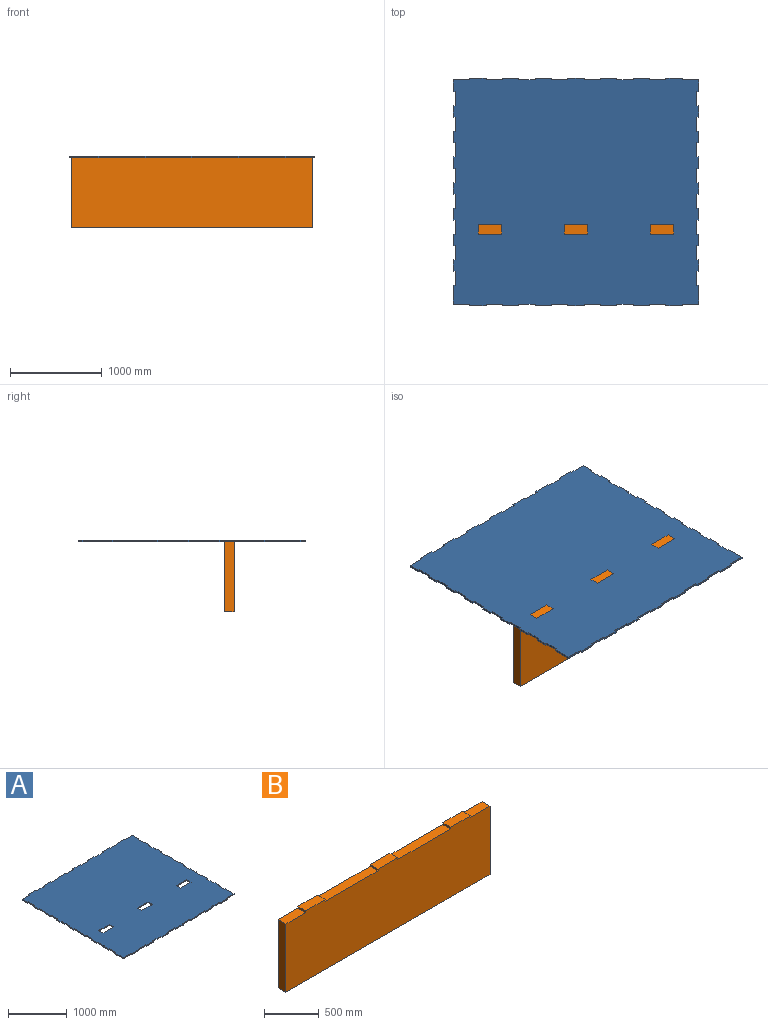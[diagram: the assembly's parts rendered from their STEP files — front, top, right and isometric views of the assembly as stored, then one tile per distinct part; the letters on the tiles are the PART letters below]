
ASSEMBLY  parts=2 mates=1
PART A: 138 faces, bbox 2667x2476.5x19.1 mm
  f0: plane 177.8x19.05mm, normal (0,-1,0), area 3387.1mm2, adj f22,f31,f133,f135
  f1: plane 177.8x19.05mm, normal (0,-1,0), area 3387.1mm2, adj f22,f31,f130,f132
  f2: plane 177.8x19.05mm, normal (0,-1,0), area 3387.1mm2, adj f22,f31,f127,f129
  f3: plane 177.8x19.05mm, normal (0,-1,0), area 3387.1mm2, adj f22,f31,f124,f126
  f4: plane 177.8x19.05mm, normal (0,-1,0), area 3387.1mm2, adj f22,f31,f121,f123
  f5: plane 177.8x19.05mm, normal (0,-1,0), area 3387.1mm2, adj f22,f31,f118,f120
  f6: plane 177.8x19.05mm, normal (0,-1,0), area 3387.1mm2, adj f22,f31,f32,f117
  f7: plane 177.8x19.05mm, normal (0,1,0), area 3387.1mm2, adj f14,f22,f31,f115
  f8: plane 177.8x19.05mm, normal (0,1,0), area 3387.1mm2, adj f22,f31,f112,f114
  f9: plane 177.8x19.05mm, normal (0,1,0), area 3387.1mm2, adj f22,f31,f109,f111
  f10: plane 177.8x19.05mm, normal (0,1,0), area 3387.1mm2, adj f22,f31,f106,f108
  f11: plane 177.8x19.05mm, normal (0,1,0), area 3387.1mm2, adj f22,f31,f103,f105
  f12: plane 177.8x19.05mm, normal (0,1,0), area 3387.1mm2, adj f22,f31,f100,f102
  f13: plane 177.8x19.05mm, normal (0,1,0), area 3387.1mm2, adj f22,f31,f97,f99
  f14: plane 127x19.05mm, normal (-1,0,0), area 2419.4mm2, adj f7,f22,f31,f93
  f15: plane 127x19.05mm, normal (-1,0,0), area 2419.3mm2, adj f22,f31,f90,f94
  f16: plane 127x19.05mm, normal (-1,0,0), area 2419.3mm2, adj f22,f31,f87,f91
  f17: plane 127x19.05mm, normal (-1,0,0), area 2419.3mm2, adj f22,f31,f84,f88
  f18: plane 127x19.05mm, normal (-1,0,0), area 2419.3mm2, adj f22,f31,f81,f85
  f19: plane 127x19.05mm, normal (-1,0,0), area 2419.4mm2, adj f22,f31,f78,f82
  f20: plane 127x19.05mm, normal (-1,0,0), area 2419.3mm2, adj f22,f31,f75,f79
  f21: plane 127x19.05mm, normal (-1,0,0), area 2419.3mm2, adj f22,f31,f72,f76
  f22: plane 2667x2476.5mm, normal (0,0,1), area 6426761.3mm2, adj f0,f1,f2,f3,f4,f5,f6,f7
  f23: plane 127x19.05mm, normal (1,0,0), area 2419.3mm2, adj f22,f31,f66,f70
  f24: plane 127x19.05mm, normal (1,0,0), area 2419.3mm2, adj f22,f31,f63,f67
  f25: plane 127x19.05mm, normal (1,0,0), area 2419.3mm2, adj f22,f31,f60,f64
  f26: plane 127x19.05mm, normal (1,0,0), area 2419.3mm2, adj f22,f31,f57,f61
  f27: plane 127x19.05mm, normal (1,0,0), area 2419.4mm2, adj f22,f31,f54,f58
  f28: plane 127x19.05mm, normal (1,0,0), area 2419.3mm2, adj f22,f31,f51,f55
  f29: plane 127x19.05mm, normal (1,0,0), area 2419.3mm2, adj f22,f31,f48,f52
  f30: plane 203.2x19.05mm, normal (1,0,0), area 3871mm2, adj f22,f31,f33,f49
  f31: plane 2667x2476.5mm, normal (0,0,-1), area 6426761.3mm2, adj f0,f1,f2,f3,f4,f5,f6,f7
  f32: plane 203.2x19.05mm, normal (-1,0,0), area 3871mm2, adj f6,f22,f31,f73
  f33: plane 177.8x19.05mm, normal (0,-1,0), area 3387.1mm2, adj f22,f30,f31,f136
  f34: plane 127x19.05mm, normal (1,0,0), area 2419.4mm2, adj f22,f31,f35,f69
  f35: plane 177.8x19.05mm, normal (0,1,0), area 3387.1mm2, adj f22,f31,f34,f96
  f36: plane 101.6x19.05mm, normal (-1,0,0), area 1935.5mm2, adj f22,f31,f37,f39
  f37: plane 254x19.05mm, normal (0,1,0), area 4838.7mm2, adj f22,f31,f36,f38
  f38: plane 101.6x19.05mm, normal (1,0,0), area 1935.5mm2, adj f22,f31,f37,f39
  f39: plane 254x19.05mm, normal (0,-1,0), area 4838.7mm2, adj f22,f31,f36,f38
  f40: plane 101.6x19.05mm, normal (-1,0,0), area 1935.5mm2, adj f22,f31,f41,f43
  f41: plane 254x19.05mm, normal (0,1,0), area 4838.7mm2, adj f22,f31,f40,f42
  f42: plane 101.6x19.05mm, normal (1,0,0), area 1935.5mm2, adj f22,f31,f41,f43
  f43: plane 254x19.05mm, normal (0,-1,0), area 4838.7mm2, adj f22,f31,f40,f42
  f44: plane 101.6x19.05mm, normal (-1,0,0), area 1935.5mm2, adj f22,f31,f45,f47
  f45: plane 254x19.05mm, normal (0,1,0), area 4838.7mm2, adj f22,f31,f44,f46
  f46: plane 101.6x19.05mm, normal (1,0,0), area 1935.5mm2, adj f22,f31,f45,f47
  f47: plane 254x19.05mm, normal (0,-1,0), area 4838.7mm2, adj f22,f31,f44,f46
  f48: plane 19.05x19.05mm, normal (0,-1,0), area 362.9mm2, adj f22,f29,f31,f50
  f49: plane 19.05x19.05mm, normal (0,1,0), area 362.9mm2, adj f22,f30,f31,f50
  f50: plane 152.4x19.05mm, normal (1,0,0), area 2903.2mm2, adj f22,f31,f48,f49
  f51: plane 19.05x19.05mm, normal (0,-1,0), area 362.9mm2, adj f22,f28,f31,f53
  f52: plane 19.05x19.05mm, normal (0,1,0), area 362.9mm2, adj f22,f29,f31,f53
  f53: plane 152.4x19.05mm, normal (1,0,0), area 2903.2mm2, adj f22,f31,f51,f52
  f54: plane 19.05x19.05mm, normal (0,-1,0), area 362.9mm2, adj f22,f27,f31,f56
  f55: plane 19.05x19.05mm, normal (0,1,0), area 362.9mm2, adj f22,f28,f31,f56
  f56: plane 152.4x19.05mm, normal (1,0,0), area 2903.2mm2, adj f22,f31,f54,f55
  f57: plane 19.05x19.05mm, normal (0,-1,0), area 362.9mm2, adj f22,f26,f31,f59
  f58: plane 19.05x19.05mm, normal (0,1,0), area 362.9mm2, adj f22,f27,f31,f59
  f59: plane 152.4x19.05mm, normal (1,0,0), area 2903.2mm2, adj f22,f31,f57,f58
  f60: plane 19.05x19.05mm, normal (0,-1,0), area 362.9mm2, adj f22,f25,f31,f62
  f61: plane 19.05x19.05mm, normal (0,1,0), area 362.9mm2, adj f22,f26,f31,f62
  f62: plane 152.4x19.05mm, normal (1,0,0), area 2903.2mm2, adj f22,f31,f60,f61
  f63: plane 19.05x19.05mm, normal (0,-1,0), area 362.9mm2, adj f22,f24,f31,f65
  f64: plane 19.05x19.05mm, normal (0,1,0), area 362.9mm2, adj f22,f25,f31,f65
  f65: plane 152.4x19.05mm, normal (1,0,0), area 2903.2mm2, adj f22,f31,f63,f64
  f66: plane 19.05x19.05mm, normal (0,-1,0), area 362.9mm2, adj f22,f23,f31,f68
  f67: plane 19.05x19.05mm, normal (0,1,0), area 362.9mm2, adj f22,f24,f31,f68
  f68: plane 152.4x19.05mm, normal (1,0,0), area 2903.2mm2, adj f22,f31,f66,f67
  f69: plane 19.05x19.05mm, normal (0,-1,0), area 362.9mm2, adj f22,f31,f34,f71
  f70: plane 19.05x19.05mm, normal (0,1,0), area 362.9mm2, adj f22,f23,f31,f71
  f71: plane 152.4x19.05mm, normal (1,0,0), area 2903.2mm2, adj f22,f31,f69,f70
  f72: plane 19.05x19.05mm, normal (0,-1,0), area 362.9mm2, adj f21,f22,f31,f74
  f73: plane 19.05x19.05mm, normal (0,1,0), area 362.9mm2, adj f22,f31,f32,f74
  f74: plane 152.4x19.05mm, normal (-1,0,0), area 2903.2mm2, adj f22,f31,f72,f73
  f75: plane 19.05x19.05mm, normal (0,-1,0), area 362.9mm2, adj f20,f22,f31,f77
  f76: plane 19.05x19.05mm, normal (0,1,0), area 362.9mm2, adj f21,f22,f31,f77
  f77: plane 152.4x19.05mm, normal (-1,0,0), area 2903.2mm2, adj f22,f31,f75,f76
  f78: plane 19.05x19.05mm, normal (0,-1,0), area 362.9mm2, adj f19,f22,f31,f80
  f79: plane 19.05x19.05mm, normal (0,1,0), area 362.9mm2, adj f20,f22,f31,f80
  f80: plane 152.4x19.05mm, normal (-1,0,0), area 2903.2mm2, adj f22,f31,f78,f79
  f81: plane 19.05x19.05mm, normal (0,-1,0), area 362.9mm2, adj f18,f22,f31,f83
  f82: plane 19.05x19.05mm, normal (0,1,0), area 362.9mm2, adj f19,f22,f31,f83
  f83: plane 152.4x19.05mm, normal (-1,0,0), area 2903.2mm2, adj f22,f31,f81,f82
  f84: plane 19.05x19.05mm, normal (0,-1,0), area 362.9mm2, adj f17,f22,f31,f86
  f85: plane 19.05x19.05mm, normal (0,1,0), area 362.9mm2, adj f18,f22,f31,f86
  f86: plane 152.4x19.05mm, normal (-1,0,0), area 2903.2mm2, adj f22,f31,f84,f85
  f87: plane 19.05x19.05mm, normal (0,-1,0), area 362.9mm2, adj f16,f22,f31,f89
  f88: plane 19.05x19.05mm, normal (0,1,0), area 362.9mm2, adj f17,f22,f31,f89
  f89: plane 152.4x19.05mm, normal (-1,0,0), area 2903.2mm2, adj f22,f31,f87,f88
  f90: plane 19.05x19.05mm, normal (0,-1,0), area 362.9mm2, adj f15,f22,f31,f92
  f91: plane 19.05x19.05mm, normal (0,1,0), area 362.9mm2, adj f16,f22,f31,f92
  f92: plane 152.4x19.05mm, normal (-1,0,0), area 2903.2mm2, adj f22,f31,f90,f91
  f93: plane 19.05x19.05mm, normal (0,-1,0), area 362.9mm2, adj f14,f22,f31,f95
  f94: plane 19.05x19.05mm, normal (0,1,0), area 362.9mm2, adj f15,f22,f31,f95
  f95: plane 152.4x19.05mm, normal (-1,0,0), area 2903.2mm2, adj f22,f31,f93,f94
  f96: plane 19.05x19.05mm, normal (1,0,0), area 362.9mm2, adj f22,f31,f35,f98
  f97: plane 19.05x19.05mm, normal (-1,0,0), area 362.9mm2, adj f13,f22,f31,f98
  f98: plane 177.8x19.05mm, normal (0,1,0), area 3387.1mm2, adj f22,f31,f96,f97
  f99: plane 19.05x19.05mm, normal (1,0,0), area 362.9mm2, adj f13,f22,f31,f101
  f100: plane 19.05x19.05mm, normal (-1,0,0), area 362.9mm2, adj f12,f22,f31,f101
  f101: plane 177.8x19.05mm, normal (0,1,0), area 3387.1mm2, adj f22,f31,f99,f100
  f102: plane 19.05x19.05mm, normal (1,0,0), area 362.9mm2, adj f12,f22,f31,f104
  f103: plane 19.05x19.05mm, normal (-1,0,0), area 362.9mm2, adj f11,f22,f31,f104
  f104: plane 177.8x19.05mm, normal (0,1,0), area 3387.1mm2, adj f22,f31,f102,f103
  f105: plane 19.05x19.05mm, normal (1,0,0), area 362.9mm2, adj f11,f22,f31,f107
  f106: plane 19.05x19.05mm, normal (-1,0,0), area 362.9mm2, adj f10,f22,f31,f107
  f107: plane 177.8x19.05mm, normal (0,1,0), area 3387.1mm2, adj f22,f31,f105,f106
  f108: plane 19.05x19.05mm, normal (1,0,0), area 362.9mm2, adj f10,f22,f31,f110
  f109: plane 19.05x19.05mm, normal (-1,0,0), area 362.9mm2, adj f9,f22,f31,f110
  f110: plane 177.8x19.05mm, normal (0,1,0), area 3387.1mm2, adj f22,f31,f108,f109
  f111: plane 19.05x19.05mm, normal (1,0,0), area 362.9mm2, adj f9,f22,f31,f113
  f112: plane 19.05x19.05mm, normal (-1,0,0), area 362.9mm2, adj f8,f22,f31,f113
  f113: plane 177.8x19.05mm, normal (0,1,0), area 3387.1mm2, adj f22,f31,f111,f112
  f114: plane 19.05x19.05mm, normal (1,0,0), area 362.9mm2, adj f8,f22,f31,f116
  f115: plane 19.05x19.05mm, normal (-1,0,0), area 362.9mm2, adj f7,f22,f31,f116
  f116: plane 177.8x19.05mm, normal (0,1,0), area 3387.1mm2, adj f22,f31,f114,f115
  f117: plane 19.05x19.05mm, normal (-1,0,0), area 362.9mm2, adj f6,f22,f31,f119
  f118: plane 19.05x19.05mm, normal (1,0,0), area 362.9mm2, adj f5,f22,f31,f119
  f119: plane 177.8x19.05mm, normal (0,-1,0), area 3387.1mm2, adj f22,f31,f117,f118
  f120: plane 19.05x19.05mm, normal (-1,0,0), area 362.9mm2, adj f5,f22,f31,f122
  f121: plane 19.05x19.05mm, normal (1,0,0), area 362.9mm2, adj f4,f22,f31,f122
  f122: plane 177.8x19.05mm, normal (0,-1,0), area 3387.1mm2, adj f22,f31,f120,f121
  f123: plane 19.05x19.05mm, normal (-1,0,0), area 362.9mm2, adj f4,f22,f31,f125
  f124: plane 19.05x19.05mm, normal (1,0,0), area 362.9mm2, adj f3,f22,f31,f125
  f125: plane 177.8x19.05mm, normal (0,-1,0), area 3387.1mm2, adj f22,f31,f123,f124
  f126: plane 19.05x19.05mm, normal (-1,0,0), area 362.9mm2, adj f3,f22,f31,f128
  f127: plane 19.05x19.05mm, normal (1,0,0), area 362.9mm2, adj f2,f22,f31,f128
  f128: plane 177.8x19.05mm, normal (0,-1,0), area 3387.1mm2, adj f22,f31,f126,f127
  f129: plane 19.05x19.05mm, normal (-1,0,0), area 362.9mm2, adj f2,f22,f31,f131
  f130: plane 19.05x19.05mm, normal (1,0,0), area 362.9mm2, adj f1,f22,f31,f131
  f131: plane 177.8x19.05mm, normal (0,-1,0), area 3387.1mm2, adj f22,f31,f129,f130
  f132: plane 19.05x19.05mm, normal (-1,0,0), area 362.9mm2, adj f1,f22,f31,f134
  f133: plane 19.05x19.05mm, normal (1,0,0), area 362.9mm2, adj f0,f22,f31,f134
  f134: plane 177.8x19.05mm, normal (0,-1,0), area 3387.1mm2, adj f22,f31,f132,f133
  f135: plane 19.05x19.05mm, normal (-1,0,0), area 362.9mm2, adj f0,f22,f31,f137
  f136: plane 19.05x19.05mm, normal (1,0,0), area 362.9mm2, adj f22,f31,f33,f137
  f137: plane 177.8x19.05mm, normal (0,-1,0), area 3387.1mm2, adj f22,f31,f135,f136
PART B: 18 faces, bbox 2628.9x101.6x781.1 mm
  f0: plane 679.45x101.6mm, normal (0,0,1), area 69032.1mm2, adj f4,f6,f13,f15
  f1: plane 679.45x101.6mm, normal (0,0,1), area 69032.1mm2, adj f4,f6,f10,f12
  f2: plane 254x101.6mm, normal (0,0,1), area 25806.4mm2, adj f3,f4,f6,f9
  f3: plane 762x101.6mm, normal (-1,0,0), area 77419.2mm2, adj f2,f4,f6,f8
  f4: plane 2628.9x781.05mm, normal (0,-1,0), area 2017737.9mm2, adj f0,f1,f2,f3,f5,f7,f8,f9
  f5: plane 762x101.6mm, normal (1,0,0), area 77419.2mm2, adj f4,f6,f7,f8
  f6: plane 2628.9x781.05mm, normal (0,1,0), area 2017737.9mm2, adj f0,f1,f2,f3,f5,f7,f8,f9
  f7: plane 254x101.6mm, normal (0,0,1), area 25806.4mm2, adj f4,f5,f6,f16
  f8: plane 2628.9x101.6mm, normal (0,0,-1), area 267096.2mm2, adj f3,f4,f5,f6
  f9: plane 101.6x19.05mm, normal (-1,0,0), area 1935.5mm2, adj f2,f4,f6,f11
  f10: plane 101.6x19.05mm, normal (1,0,0), area 1935.5mm2, adj f1,f4,f6,f11
  f11: plane 254x101.6mm, normal (0,0,1), area 25806.4mm2, adj f4,f6,f9,f10
  f12: plane 101.6x19.05mm, normal (-1,0,0), area 1935.5mm2, adj f1,f4,f6,f14
  f13: plane 101.6x19.05mm, normal (1,0,0), area 1935.5mm2, adj f0,f4,f6,f14
  f14: plane 254x101.6mm, normal (0,0,1), area 25806.4mm2, adj f4,f6,f12,f13
  f15: plane 101.6x19.05mm, normal (-1,0,0), area 1935.5mm2, adj f0,f4,f6,f17
  f16: plane 101.6x19.05mm, normal (1,0,0), area 1935.5mm2, adj f4,f6,f7,f17
  f17: plane 254x101.6mm, normal (0,0,1), area 25806.4mm2, adj f4,f6,f15,f16
PLACE A t=(-403.38,-438.04,340.21)mm
PLACE B t=(-384.33,323.96,-421.79)mm
MATE fastened B.f14 <-> A.f22  axis (0,0,1) through (930.12,425.56,359.26)mm
